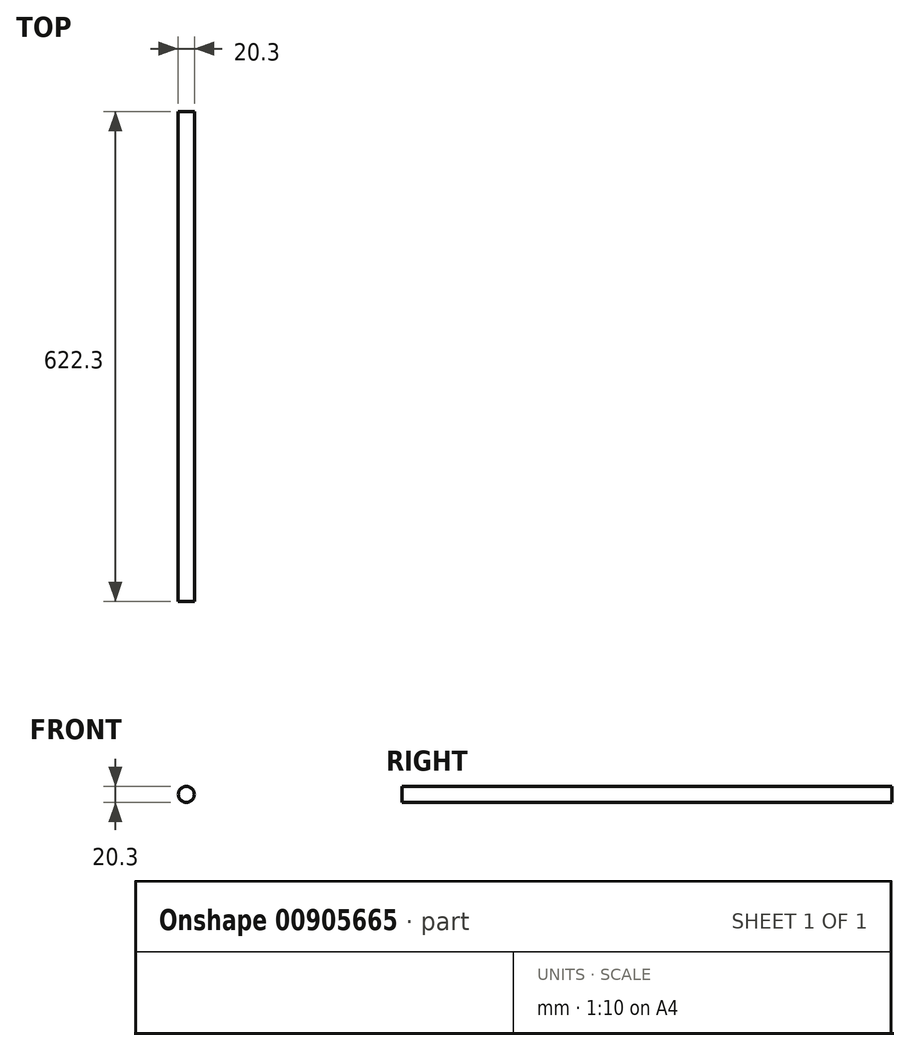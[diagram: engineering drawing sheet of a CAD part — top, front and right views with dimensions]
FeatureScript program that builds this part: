
annotation { "Feature Type Name" : "Feature", "Feature Type Description" : "" }
export const myFeature = defineFeature(function(context is Context, id is Id, definition is map)
    precondition{}
    {
        {
            var Q0;
            Q0=qCreatedBy(makeId("Front.planeOp"),FACE);
            var sketch = newSketch(context, id + "F0", { "sketchPlane" : qUnion([Q0])});
            skCircle(sketch, "E0", {"center": v(0, 0) * mm, "radius": 10.15 * mm});
            skSolve(sketch);
        }
        {
            var Q0;
            Q0=qSketchRegion(id+"F0",true);
            extrude(context, id + "F1", {"entities" : qUnion([Q0]), "depth" : 311.15 * mm, "offsetDistance" : 25.4 * mm, "hasSecondDirection" : true, "secondDirectionOppositeDirection" : true, "secondDirectionDepth" : 311.15 * mm});
        }
    });
